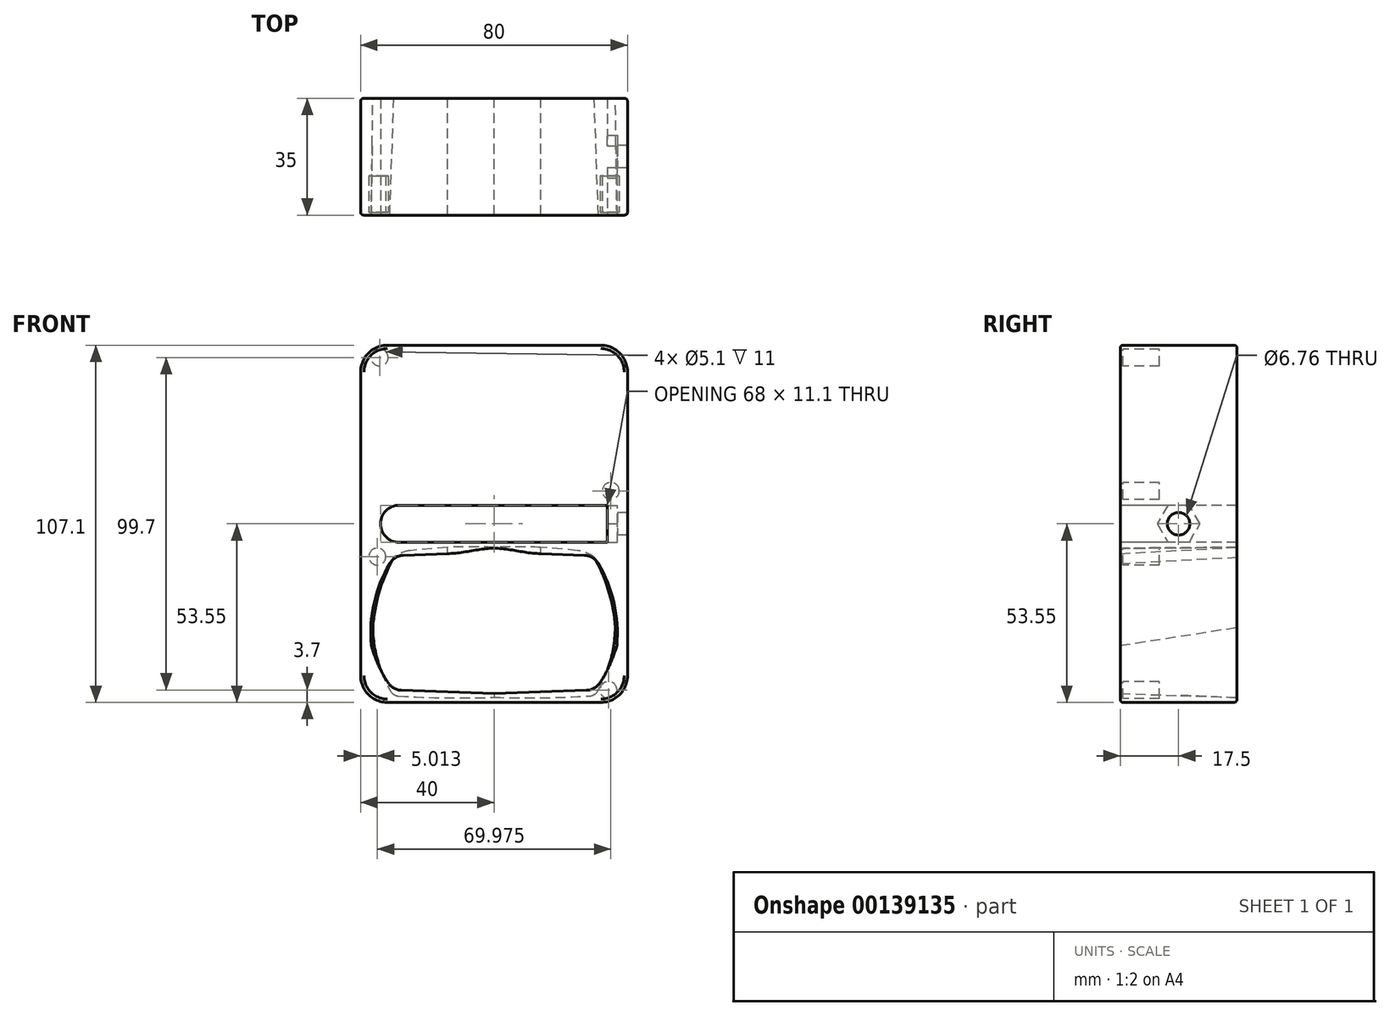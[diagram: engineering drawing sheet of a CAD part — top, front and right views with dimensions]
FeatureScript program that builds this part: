
annotation { "Feature Type Name" : "Feature", "Feature Type Description" : "" }
export const myFeature = defineFeature(function(context is Context, id is Id, definition is map)
    precondition{}
    {
        {
            var Q0;
            Q0=qCreatedBy(makeId("Front.planeOp"),FACE);
            var sketch = newSketch(context, id + "F0", { "sketchPlane" : qUnion([Q0])});
            skLineSegment(sketch, "E0.bottom", {"start": v(-40, 24.5) * mm, "end": v(40, 24.5) * mm});
            skLineSegment(sketch, "E0.top", {"start": v(-40, -23.5) * mm, "end": v(40, -23.5) * mm});
            skLineSegment(sketch, "E0.left", {"start": v(-40, 24.5) * mm, "end": v(-40, -23.5) * mm});
            skLineSegment(sketch, "E0.right", {"start": v(40, 24.5) * mm, "end": v(40, -23.5) * mm});
            skLineSegment(sketch, "E1.bottom", {"start": v(-40, 24.5) * mm, "end": v(40, 24.5) * mm, "construction": true});
            skLineSegment(sketch, "E1.top", {"start": v(-40, 35.6) * mm, "end": v(40, 35.6) * mm});
            skLineSegment(sketch, "E1.left", {"start": v(-40, 24.5) * mm, "end": v(-40, 35.6) * mm});
            skLineSegment(sketch, "E2.right", {"start": v(40, 24.5) * mm, "end": v(40, -23.5) * mm, "construction": true});
            skLineSegment(sketch, "E3.top", {"start": v(-40, 83.6) * mm, "end": v(40, 83.6) * mm});
            skLineSegment(sketch, "E3.left", {"start": v(-40, 35.6) * mm, "end": v(-40, 83.6) * mm});
            skLineSegment(sketch, "E3.right", {"start": v(40, 35.6) * mm, "end": v(40, 83.6) * mm});
            skLineSegment(sketch, "E4", {"start": v(40, 24.5) * mm, "end": v(40, 35.6) * mm});
            skLineSegment(sketch, "E5", {"start": v(-34, 24.5) * mm, "end": v(-34, 35.6) * mm});
            skLineSegment(sketch, "E6", {"start": v(37, 24.5) * mm, "end": v(37, 35.6) * mm});
            skSolve(sketch);
        }
        {
            var Q0;
            Q0=qSketchRegion(id+"F0",true);
            extrude(context, id + "F1", {"entities" : qUnion([Q0]), "oppositeDirection" : true, "depth" : 35 * mm});
        }
        {
            var Q0;
            Q0=qCreatedBy(makeId("Front.planeOp"),FACE);
            var sketch = newSketch(context, id + "F2", { "sketchPlane" : qUnion([Q0])});
            skLineSegment(sketch, "E7.bottom", {"start": v(13.97, 21.11) * mm, "end": v(-16.03, 21.11) * mm, "construction": true});
            skLineSegment(sketch, "E7.top", {"start": v(13.97, 22.71) * mm, "end": v(0, 22.71) * mm, "construction": true});
            skLineSegment(sketch, "E7.left", {"start": v(13.97, 21.11) * mm, "end": v(13.97, 22.71) * mm, "construction": true});
            skPoint(sketch, "E8", {"position": v(29.75, 20.51) * mm});
            skPoint(sketch, "E9", {"position": v(36.8, -6.39) * mm});
            skLineSegment(sketch, "E10", {"start": v(27.14, 20.61) * mm, "end": v(13.97, 21.11) * mm});
            skArc(sketch, "E11", {"start": v(36.8, -6.39) * mm, "mid": v(35.96, 6.32) * mm, "end": v(31.25, 18.16) * mm});
            skArc(sketch, "E12.filletArc", {"start": v(31.25, 18.16) * mm, "mid": v(29.5, 19.91) * mm, "end": v(27.14, 20.61) * mm});
            skPoint(sketch, "E13.visualSharp", {"position": v(30.23, -19.8) * mm});
            skLineSegment(sketch, "E14", {"start": v(0, 22.71) * mm, "end": v(-13.97, 22.71) * mm, "construction": true});
            skLineSegment(sketch, "E15.trimOffspring", {"start": v(27.14, 20.61) * mm, "end": v(29.75, 20.51) * mm, "construction": true});
            skLineSegment(sketch, "E16", {"start": v(0, -20.89) * mm, "end": v(27.75, -19.89) * mm});
            skArc(sketch, "E17", {"start": v(31.76, -17.62) * mm, "mid": v(34.71, -12.2) * mm, "end": v(36.8, -6.39) * mm});
            skArc(sketch, "E18.filletArc", {"start": v(27.75, -19.89) * mm, "mid": v(30.03, -19.24) * mm, "end": v(31.76, -17.62) * mm});
            skLineSegment(sketch, "E19.MirrorCS", {"start": v(-27.14, 20.61) * mm, "end": v(-13.97, 21.11) * mm});
            skArc(sketch, "E20.MirrorCS", {"start": v(-31.25, 18.16) * mm, "mid": v(-29.5, 19.91) * mm, "end": v(-27.14, 20.61) * mm});
            skArc(sketch, "E21.MirrorCS", {"start": v(-36.8, -6.39) * mm, "mid": v(-35.96, 6.32) * mm, "end": v(-31.25, 18.16) * mm});
            skArc(sketch, "E22.MirrorCS", {"start": v(-31.76, -17.62) * mm, "mid": v(-34.71, -12.2) * mm, "end": v(-36.8, -6.39) * mm});
            skArc(sketch, "E23.MirrorCS", {"start": v(-27.75, -19.89) * mm, "mid": v(-30.03, -19.24) * mm, "end": v(-31.76, -17.62) * mm});
            skLineSegment(sketch, "E24.MirrorCS", {"start": v(0, -20.89) * mm, "end": v(-27.75, -19.89) * mm});
            skLineSegment(sketch, "E25", {"start": v(0, -20.89) * mm, "end": v(37, -20.89) * mm, "construction": true});
            skFitSpline(sketch, "E26", {"points": [v(0, 22.71) * mm, v(13.97, 21.11) * mm], "startDerivative": vector(13.88, 0) * mm, "endDerivative": vector(13.88, 0) * mm});
            skFitSpline(sketch, "E27.MirrorCS", {"points": [v(0, 22.71) * mm, v(-13.97, 21.11) * mm], "startDerivative": vector(-13.88, 0) * mm, "endDerivative": vector(-13.88, 0) * mm});
            skSolve(sketch);
        }
        {
            var Q0;
            Q0=makeQuery(id+"F2.imprint","IMPRINT",FACE,{"disambiguationData":[TD([[makeQuery(id+"F2.imprint","IMPRINT",EDGE,{"derivedFrom":sQuery(id+"F2.wireOp",EDGE,"E10")}),1.0]])]});
            cPlane(context, id + "F3", {"entities" : qUnion([Q0]), "cplaneType" : CPlaneType.OFFSET, "offset" : 35 * mm, "oppositeDirection" : true, "width" : 150 * mm, "height" : 150 * mm});
        }
        {
            var Q0;
            Q0=qCreatedBy(id+"F3.planeOp",FACE);
            var sketch = newSketch(context, id + "F4", { "sketchPlane" : qUnion([Q0])});
            skLineSegment(sketch, "E28.bottom", {"start": v(-36.36, 23) * mm, "end": v(36.36, 23) * mm, "construction": true});
            skLineSegment(sketch, "E28.top", {"start": v(-36.36, -22) * mm, "end": v(36.36, -22) * mm, "construction": true});
            skLineSegment(sketch, "E28.left", {"start": v(-36.36, 23) * mm, "end": v(-36.36, -22) * mm, "construction": true});
            skLineSegment(sketch, "E28.right", {"start": v(36.36, 23) * mm, "end": v(36.36, -22) * mm, "construction": true});
            skPoint(sketch, "E29", {"position": v(0, 23) * mm});
            skPoint(sketch, "E30", {"position": v(0, -22) * mm});
            skPoint(sketch, "E31", {"position": v(-36.36, -1) * mm});
            skPoint(sketch, "E32.MirrorP", {"position": v(36.36, -1) * mm});
            skPoint(sketch, "E33", {"position": v(30.23, -21.5) * mm});
            skPoint(sketch, "E34.0", {"position": v(29.75, 20.51) * mm});
            skArc(sketch, "E35", {"start": v(36.36, -1) * mm, "mid": v(34.36, 9.85) * mm, "end": v(30.04, 20) * mm});
            skArc(sketch, "E36", {"start": v(31.08, -20.1) * mm, "mid": v(34.92, -10.88) * mm, "end": v(36.36, -1) * mm});
            skArc(sketch, "E37", {"start": v(0, -22) * mm, "mid": v(14.33, -22.13) * mm, "end": v(28.66, -21.6) * mm});
            skArc(sketch, "E38.filletArc", {"start": v(28.66, -21.6) * mm, "mid": v(30.06, -21.15) * mm, "end": v(31.08, -20.1) * mm});
            skArc(sketch, "E39.MirrorCS", {"start": v(-36.36, -1) * mm, "mid": v(-34.36, 9.85) * mm, "end": v(-30.04, 20) * mm});
            skArc(sketch, "E40.MirrorCS", {"start": v(-31.08, -20.1) * mm, "mid": v(-34.92, -10.88) * mm, "end": v(-36.36, -1) * mm});
            skArc(sketch, "E41.MirrorCS", {"start": v(-28.66, -21.6) * mm, "mid": v(-30.06, -21.15) * mm, "end": v(-31.08, -20.1) * mm});
            skArc(sketch, "E42.MirrorCS", {"start": v(0, -22) * mm, "mid": v(-14.33, -22.13) * mm, "end": v(-28.66, -21.6) * mm});
            skArc(sketch, "E43", {"start": v(14, 23) * mm, "mid": v(7, 23.07) * mm, "end": v(0, 23) * mm});
            skArc(sketch, "E44", {"start": v(-14, 23) * mm, "mid": v(-7, 23.07) * mm, "end": v(0, 23) * mm});
            skLineSegment(sketch, "E45", {"start": v(25.06, 22) * mm, "end": v(14, 23) * mm});
            skLineSegment(sketch, "E46", {"start": v(-14, 23) * mm, "end": v(-25.06, 22) * mm});
            skArc(sketch, "E47", {"start": v(25.06, 22) * mm, "mid": v(27.7, 21.37) * mm, "end": v(30.04, 20) * mm});
            skArc(sketch, "E48.MirrorCS", {"start": v(-25.06, 22) * mm, "mid": v(-27.7, 21.37) * mm, "end": v(-30.04, 20) * mm});
            skSolve(sketch);
        }
        {
            var Q1;
            Q1=makeQuery(id+"F2.imprint","IMPRINT",FACE,{"disambiguationData":[TD([[makeQuery(id+"F2.imprint","IMPRINT",EDGE,{"derivedFrom":sQuery(id+"F2.wireOp",EDGE,"E10")}),1.0]])]});
            var Q2;
            Q2=makeQuery(id+"F4.imprint","IMPRINT",FACE,{"disambiguationData":[TD([[makeQuery(id+"F4.imprint","IMPRINT",EDGE,{"derivedFrom":sQuery(id+"F4.wireOp",EDGE,"E35")}),1.0]])]});
            loft(context, id + "F5", {"operationType" : NewBodyOperationType.REMOVE, "sheetProfilesArray" : [{ "sheetProfileEntities" : qUnion([Q1]) }, { "sheetProfileEntities" : qUnion([Q2]) }]});
        }
        {
            var Q0;
            Q0=makeQuery(id+"F1.opExtrude","SWEPT_EDGE",EDGE,{"disambiguationData":[OSD([sQuery(id+"F0.wireOp",EDGE,"E0.top"),sQuery(id+"F0.wireOp",EDGE,"E0.right")])]});
            var Q1;
            Q1=makeQuery(id+"F1.opExtrude","SWEPT_EDGE",EDGE,{"disambiguationData":[OSD([sQuery(id+"F0.wireOp",EDGE,"E0.top"),sQuery(id+"F0.wireOp",EDGE,"E0.left")])]});
            var Q2;
            Q2=makeQuery(id+"F1.opExtrude","SWEPT_EDGE",EDGE,{"disambiguationData":[OSD([sQuery(id+"F0.wireOp",EDGE,"E3.top"),sQuery(id+"F0.wireOp",EDGE,"E3.right")])]});
            var Q3;
            Q3=makeQuery(id+"F1.opExtrude","SWEPT_EDGE",EDGE,{"disambiguationData":[OSD([sQuery(id+"F0.wireOp",EDGE,"E3.top"),sQuery(id+"F0.wireOp",EDGE,"E3.left")])]});
            fillet(context, id + "F6", {"entities" : qUnion([Q0, Q1, Q2, Q3]), "radius" : 8 * mm, "tangentPropagation" : true, "allowEdgeOverflow" : false});
        }
        {
            var Q0;
            Q0=makeQuery(id+"F1.opExtrude","SWEPT_FACE",FACE,{"disambiguationData":[OSD([sQuery(id+"F0.wireOp",EDGE,"E6")])]});
            var sketch = newSketch(context, id + "F7", { "sketchPlane" : qUnion([Q0])});
            skLineSegment(sketch, "E49.0", {"start": v(0, 24.5) * mm, "end": v(0, 35.6) * mm, "construction": true});
            skLineSegment(sketch, "E50.0", {"start": v(-35, 24.5) * mm, "end": v(-35, 35.6) * mm, "construction": true});
            skPoint(sketch, "E51", {"position": v(0, 30.05) * mm});
            skLineSegment(sketch, "E52", {"start": v(0, 30.05) * mm, "end": v(-35, 30.05) * mm, "construction": true});
            skPoint(sketch, "E53", {"position": v(-17.5, 30.05) * mm});
            skCircle(sketch, "E54.cCircle", {"center": v(-17.5, 30.05) * mm, "radius": 5.55 * mm, "construction": true});
            skLineSegment(sketch, "E54.0", {"start": v(-14.3, 35.6) * mm, "end": v(-11.1, 30.05) * mm});
            skLineSegment(sketch, "E54.1", {"start": v(-11.1, 30.05) * mm, "end": v(-14.3, 24.5) * mm});
            skLineSegment(sketch, "E54.2", {"start": v(-14.3, 24.5) * mm, "end": v(-20.7, 24.5) * mm});
            skLineSegment(sketch, "E54.3", {"start": v(-20.7, 24.5) * mm, "end": v(-23.9, 30.05) * mm});
            skLineSegment(sketch, "E54.4", {"start": v(-23.9, 30.05) * mm, "end": v(-20.7, 35.6) * mm});
            skLineSegment(sketch, "E54.5", {"start": v(-20.7, 35.6) * mm, "end": v(-14.3, 35.6) * mm});
            skPoint(sketch, "E54.0.midPoint", {"position": v(-12.7, 32.82) * mm});
            skSolve(sketch);
        }
        {
            var Q0;
            Q0=sQuery(id+"F7.wireOp",VERTEX,"E53");
            var Q1;
            Q1=makeQuery(id+"F1.opExtrude","SWEPT_BODY",BODY,{"disambiguationData":[OSD([sQuery(id+"F0.wireOp",EDGE,"E0.bottom"),sQuery(id+"F0.wireOp",EDGE,"E0.top"),sQuery(id+"F0.wireOp",EDGE,"E0.left"),sQuery(id+"F0.wireOp",EDGE,"E0.right"),sQuery(id+"F0.wireOp",EDGE,"E1.left"),sQuery(id+"F0.wireOp",EDGE,"E1.top"),sQuery(id+"F0.wireOp",EDGE,"E3.top"),sQuery(id+"F0.wireOp",EDGE,"E3.left"),sQuery(id+"F0.wireOp",EDGE,"E3.right"),sQuery(id+"F0.wireOp",EDGE,"E4"),sQuery(id+"F0.wireOp",EDGE,"E5"),sQuery(id+"F0.wireOp",EDGE,"E6")])]});
            hole(context, id + "F8", {"style" : HoleStyle.SIMPLE, "endStyle" : HoleEndStyle.BLIND, "standardTappedOrClearance" : lookupTablePath({ "standard" : "ANSI", "fit" : "Normal (ASME)", "size" : "1/4", "type" : "Clearance" }), "standardBlindInLast" : lookupTablePath({ "fit" : "Free", "standard" : "ANSI", "size" : "1/4", "type" : "Clearance" }), "holeDiameter" : 6.76 * mm, "holeDepth" : 30 * mm, "startFromSketch" : true, "locations" : qUnion([Q0]), "scope" : qUnion([Q1])});
        }
        {
            var Q0;
            {var subQ5=sQuery(id+"F7.wireOp",EDGE,"E54.0");Q0=makeQuery(id+"F7.imprint","IMPRINT",FACE,{"disambiguationData":[TD([[makeQuery(id+"F7.imprint","IMPRINT",EDGE,{"derivedFrom":subQ5}),1.0]])]});}
            var Q1;
            {var subQ3=sQuery(id+"F7.wireOp",EDGE,"E54.3");Q1=makeQuery(id+"F7.imprint","IMPRINT",FACE,{"disambiguationData":[TD([[makeQuery(id+"F7.imprint","IMPRINT",EDGE,{"derivedFrom":subQ3}),1.0]])]});}
            extrude(context, id + "F9", {"entities" : qUnion([Q0, Q1]), "operationType" : NewBodyOperationType.ADD, "depth" : 3 * mm});
        }
        {
            var Q0;
            Q0=makeQuery(id+"F1.opExtrude","SWEPT_EDGE",EDGE,{"disambiguationData":[OSD([sQuery(id+"F0.wireOp",EDGE,"E0.bottom"),sQuery(id+"F0.wireOp",EDGE,"E5")])]});
            var Q1;
            Q1=makeQuery(id+"F1.opExtrude","SWEPT_EDGE",EDGE,{"disambiguationData":[OSD([sQuery(id+"F0.wireOp",EDGE,"E1.top"),sQuery(id+"F0.wireOp",EDGE,"E5")])]});
            var Q2;
            {var subQ0=sQuery(id+"F0.wireOp",EDGE,"E6");var subQ1=sQuery(id+"F0.wireOp",EDGE,"E1.top");var subQ2=makeQuery(id+"F1.opExtrude","SWEPT_EDGE",EDGE,{"disambiguationData":[OSD([subQ1,subQ0])]});Q2=makeQuery(id+"F9.opExtrude","CAP_EDGE",EDGE,{"disambiguationData":[OSD([subQ1,subQ0]),TDD([makeQuery(id+"F7.imprint","IMPRINT",EDGE,{"disambiguationData":[TD([[makeQuery(id+"F7.imprint","INTERSECT",VERTEX,{"derivedFrom":[subQ2,makeQuery(id+"F1.opExtrude","CAP_EDGE",EDGE,{"disambiguationData":[OSD([subQ0])],"isStart":true})]}),1.0]])],"derivedFrom":subQ2})])],"isStart":false});}
            var Q3;
            {var subQ0=sQuery(id+"F0.wireOp",EDGE,"E6");var subQ1=sQuery(id+"F0.wireOp",EDGE,"E1.top");var subQ2=makeQuery(id+"F1.opExtrude","SWEPT_EDGE",EDGE,{"disambiguationData":[OSD([subQ1,subQ0])]});Q3=makeQuery(id+"F9.opExtrude","CAP_EDGE",EDGE,{"disambiguationData":[OSD([subQ1,subQ0]),TDD([makeQuery(id+"F7.imprint","IMPRINT",EDGE,{"disambiguationData":[TD([[makeQuery(id+"F7.imprint","INTERSECT",VERTEX,{"derivedFrom":[subQ2,makeQuery(id+"F1.opExtrude","CAP_EDGE",EDGE,{"disambiguationData":[OSD([subQ0])],"isStart":false})]}),-1.0]])],"derivedFrom":subQ2})])],"isStart":false});}
            var Q4;
            {var subQ0=sQuery(id+"F0.wireOp",EDGE,"E6");var subQ1=sQuery(id+"F0.wireOp",EDGE,"E0.bottom");var subQ2=makeQuery(id+"F1.opExtrude","SWEPT_EDGE",EDGE,{"disambiguationData":[OSD([subQ1,subQ0])]});Q4=makeQuery(id+"F9.opExtrude","CAP_EDGE",EDGE,{"disambiguationData":[OSD([subQ1,subQ0]),TDD([makeQuery(id+"F7.imprint","IMPRINT",EDGE,{"disambiguationData":[TD([[makeQuery(id+"F7.imprint","INTERSECT",VERTEX,{"derivedFrom":[subQ2,makeQuery(id+"F1.opExtrude","CAP_EDGE",EDGE,{"disambiguationData":[OSD([subQ0])],"isStart":true})]}),1.0]])],"derivedFrom":subQ2})])],"isStart":false});}
            var Q5;
            {var subQ0=sQuery(id+"F0.wireOp",EDGE,"E6");var subQ1=sQuery(id+"F0.wireOp",EDGE,"E0.bottom");var subQ2=makeQuery(id+"F1.opExtrude","SWEPT_EDGE",EDGE,{"disambiguationData":[OSD([subQ1,subQ0])]});Q5=makeQuery(id+"F9.opExtrude","CAP_EDGE",EDGE,{"disambiguationData":[OSD([subQ1,subQ0]),TDD([makeQuery(id+"F7.imprint","IMPRINT",EDGE,{"disambiguationData":[TD([[makeQuery(id+"F7.imprint","INTERSECT",VERTEX,{"derivedFrom":[subQ2,makeQuery(id+"F1.opExtrude","CAP_EDGE",EDGE,{"disambiguationData":[OSD([subQ0])],"isStart":false})]}),-1.0]])],"derivedFrom":subQ2})])],"isStart":false});}
            fillet(context, id + "F10", {"entities" : qUnion([Q0, Q1, Q2, Q3, Q4, Q5]), "radius" : 5.5 * mm, "tangentPropagation" : true, "allowEdgeOverflow" : false});
        }
        {
            var Q0;
            Q0=qCreatedBy(makeId("Front.planeOp"),FACE);
            cPlane(context, id + "F11", {"entities" : qUnion([Q0]), "cplaneType" : CPlaneType.OFFSET, "offset" : 0.8 * mm, "oppositeDirection" : true, "width" : 150 * mm, "height" : 150 * mm});
        }
        {
            var Q0;
            Q0=qCreatedBy(makeId("Top.planeOp"),FACE);
            cPlane(context, id + "F12", {"entities" : qUnion([Q0]), "cplaneType" : CPlaneType.OFFSET, "offset" : 30.05 * mm * 2, "width" : 150 * mm, "height" : 150 * mm});
        }
        {
            var Q0;
            Q0=qCreatedBy(id+"F11.planeOp",FACE);
            var sketch = newSketch(context, id + "F13", { "sketchPlane" : qUnion([Q0])});
            skPoint(sketch, "E55", {"position": v(-34.99, 20.2) * mm});
            skPoint(sketch, "E56", {"position": v(34.3, -19.8) * mm});
            skCircle(sketch, "E57", {"center": v(-34.99, 20.2) * mm, "radius": 2.55 * mm});
            skCircle(sketch, "E58", {"center": v(34.3, -19.8) * mm, "radius": 2.55 * mm});
            skLineSegment(sketch, "E59", {"start": v(-34.99, 20.2) * mm, "end": v(0, 0) * mm, "construction": true});
            skLineSegment(sketch, "E60", {"start": v(0, 0) * mm, "end": v(34.3, -19.8) * mm, "construction": true});
            skPoint(sketch, "E61", {"position": v(0, 60.1) * mm});
            skLineSegment(sketch, "E62", {"start": v(0, 60.1) * mm, "end": v(-34.3, 79.9) * mm, "construction": true});
            skLineSegment(sketch, "E63", {"start": v(0, 60.1) * mm, "end": v(34.99, 39.9) * mm, "construction": true});
            skCircle(sketch, "E64", {"center": v(-34.3, 79.9) * mm, "radius": 2.55 * mm});
            skCircle(sketch, "E65", {"center": v(34.99, 39.9) * mm, "radius": 2.55 * mm});
            skSolve(sketch);
        }
        {
            var Q0;
            Q0=makeQuery(id+"F13.imprint","IMPRINT",FACE,{"disambiguationData":[TD([[makeQuery(id+"F13.imprint","IMPRINT",EDGE,{"derivedFrom":sQuery(id+"F13.wireOp",EDGE,"E57")}),1.0]])]});
            var Q1;
            Q1=makeQuery(id+"F13.imprint","IMPRINT",FACE,{"disambiguationData":[TD([[makeQuery(id+"F13.imprint","IMPRINT",EDGE,{"derivedFrom":sQuery(id+"F13.wireOp",EDGE,"E58")}),1.0]])]});
            var Q2;
            Q2=makeQuery(id+"F13.imprint","IMPRINT",FACE,{"disambiguationData":[TD([[makeQuery(id+"F13.imprint","IMPRINT",EDGE,{"derivedFrom":sQuery(id+"F13.wireOp",EDGE,"E64")}),1.0]])]});
            var Q3;
            Q3=makeQuery(id+"F13.imprint","IMPRINT",FACE,{"disambiguationData":[TD([[makeQuery(id+"F13.imprint","IMPRINT",EDGE,{"derivedFrom":sQuery(id+"F13.wireOp",EDGE,"E65")}),1.0]])]});
            var Q4;
            Q4=sQuery(id+"F13.wireOp",EDGE,"E57");
            var Q5;
            Q5=sQuery(id+"F13.wireOp",EDGE,"E58");
            extrude(context, id + "F14", {"entities" : qUnion([Q0, Q1, Q2, Q3]), "operationType" : NewBodyOperationType.REMOVE, "surfaceEntities" : qUnion([Q4, Q5]), "oppositeDirection" : true, "depth" : 11 * mm});
        }
        {
            var Q0;
            Q0=qCreatedBy(makeId("Top.planeOp"),FACE);
            cPlane(context, id + "F15", {"entities" : qUnion([Q0]), "cplaneType" : CPlaneType.OFFSET, "offset" : 30.05 * mm, "width" : 150 * mm, "height" : 150 * mm});
        }
        {
            var Q0;
            Q0=makeQuery(id+"F1.opExtrude","CAP_EDGE",EDGE,{"disambiguationData":[OSD([sQuery(id+"F0.wireOp",EDGE,"E0.right"),sQuery(id+"F0.wireOp",EDGE,"E3.right"),sQuery(id+"F0.wireOp",EDGE,"E4")])],"isStart":true});
            var Q1;
            Q1=makeQuery(id+"F1.opExtrude","CAP_EDGE",EDGE,{"disambiguationData":[OSD([sQuery(id+"F0.wireOp",EDGE,"E0.right"),sQuery(id+"F0.wireOp",EDGE,"E3.right"),sQuery(id+"F0.wireOp",EDGE,"E4")])],"isStart":false});
            fillet(context, id + "F16", {"entities" : qUnion([Q0, Q1]), "radius" : 1 * mm, "tangentPropagation" : true, "rho" : 0.5, "crossSection" : FilletCrossSection.CONIC, "allowEdgeOverflow" : false});
        }
    });
